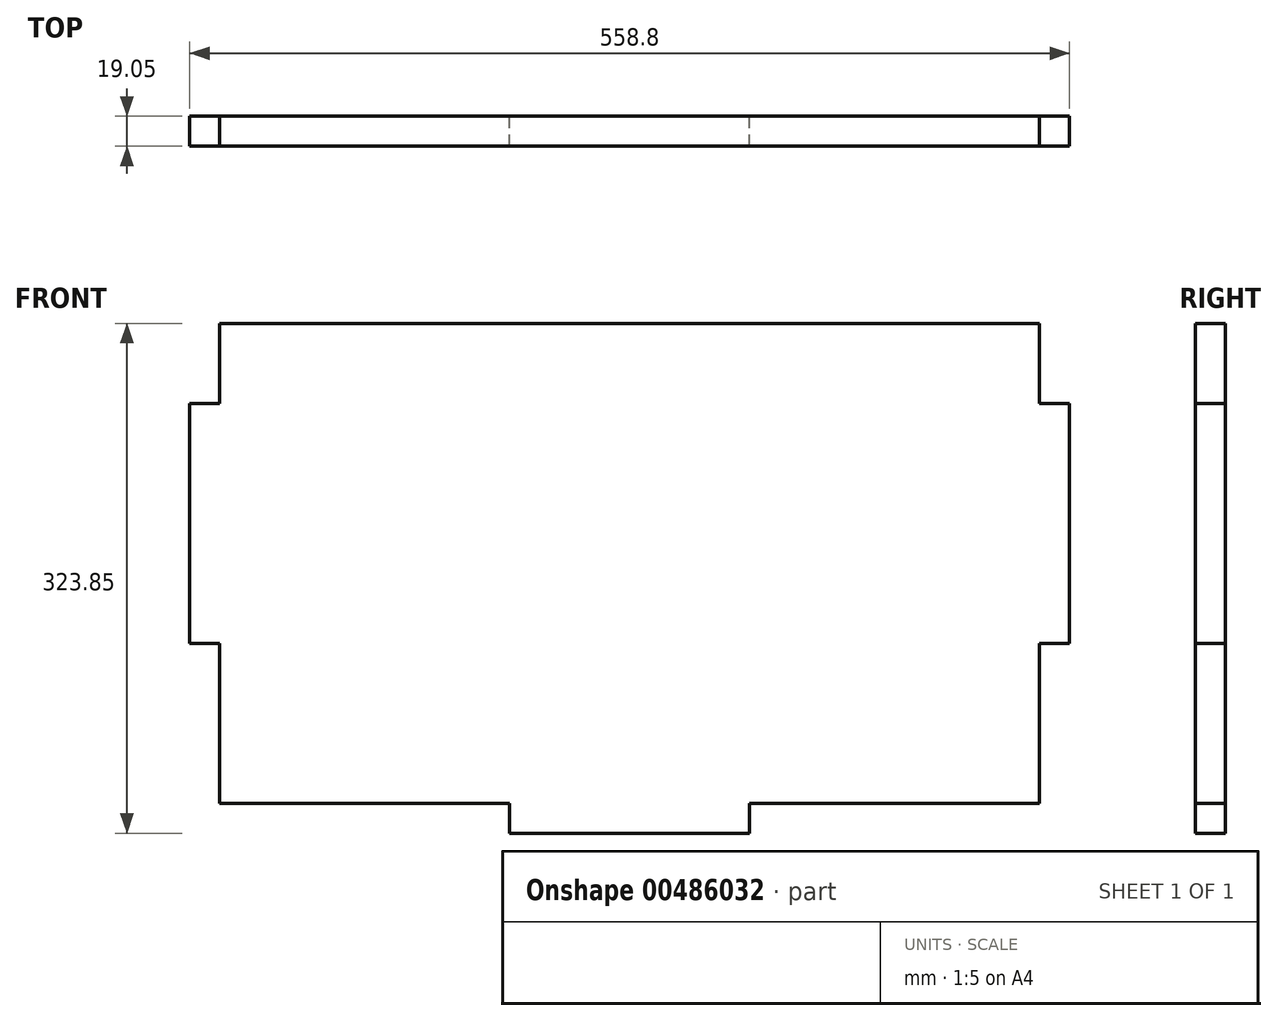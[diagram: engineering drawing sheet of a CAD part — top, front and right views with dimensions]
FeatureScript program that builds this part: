
annotation { "Feature Type Name" : "Feature", "Feature Type Description" : "" }
export const myFeature = defineFeature(function(context is Context, id is Id, definition is map)
    precondition{}
    {
        {
            var Q0;
            Q0=qCreatedBy(makeId("Front.planeOp"),FACE);
            var sketch = newSketch(context, id + "F0", { "sketchPlane" : qUnion([Q0])});
            skLineSegment(sketch, "E0.bottom", {"start": v(-204.8, -103.62) * mm, "end": v(-725.5, -103.62) * mm});
            skLineSegment(sketch, "E0.top", {"start": v(-204.8, 201.18) * mm, "end": v(-725.5, 201.18) * mm});
            skLineSegment(sketch, "E0.left", {"start": v(-204.8, -103.62) * mm, "end": v(-204.8, 201.18) * mm});
            skLineSegment(sketch, "E0.right", {"start": v(-725.5, -103.62) * mm, "end": v(-725.5, 201.18) * mm});
            skLineSegment(sketch, "E1.bottom", {"start": v(-725.5, 150.38) * mm, "end": v(-744.55, 150.38) * mm});
            skLineSegment(sketch, "E1.top", {"start": v(-725.5, -2.02) * mm, "end": v(-744.55, -2.02) * mm});
            skLineSegment(sketch, "E1.left", {"start": v(-725.5, 150.38) * mm, "end": v(-725.5, -2.02) * mm});
            skLineSegment(sketch, "E1.right", {"start": v(-744.55, 150.38) * mm, "end": v(-744.55, -2.02) * mm});
            skLineSegment(sketch, "E2.bottom", {"start": v(-204.8, 150.38) * mm, "end": v(-185.75, 150.38) * mm});
            skLineSegment(sketch, "E2.top", {"start": v(-204.8, -2.02) * mm, "end": v(-185.75, -2.02) * mm});
            skLineSegment(sketch, "E2.left", {"start": v(-204.8, 150.38) * mm, "end": v(-204.8, -2.02) * mm});
            skLineSegment(sketch, "E2.right", {"start": v(-185.75, 150.38) * mm, "end": v(-185.75, -2.02) * mm});
            skLineSegment(sketch, "E3", {"start": v(-204.8, -2.02) * mm, "end": v(-204.8, -103.62) * mm});
            skLineSegment(sketch, "E4", {"start": v(-725.5, -2.02) * mm, "end": v(-725.5, -103.62) * mm});
            skPoint(sketch, "E5.middle", {"position": v(-465.15, -103.62) * mm});
            skLineSegment(sketch, "E6", {"start": v(-725.5, -103.62) * mm, "end": v(-541.35, -103.62) * mm});
            skLineSegment(sketch, "E7", {"start": v(-204.8, -103.62) * mm, "end": v(-388.95, -103.62) * mm});
            skLineSegment(sketch, "E8", {"start": v(-541.35, -103.62) * mm, "end": v(-541.35, -122.67) * mm});
            skLineSegment(sketch, "E9", {"start": v(-541.35, -122.67) * mm, "end": v(-388.95, -122.67) * mm});
            skLineSegment(sketch, "E10", {"start": v(-388.95, -122.67) * mm, "end": v(-388.95, -103.62) * mm});
            skSolve(sketch);
        }
        {
            var Q0;
            {var subQ3=sQuery(id+"F0.wireOp",EDGE,"E0.bottom");Q0=makeQuery(id+"F0.imprint","IMPRINT",FACE,{"disambiguationData":[TD([[makeQuery(id+"F0.imprint","IMPRINT",EDGE,{"derivedFrom":subQ3}),-1.0]])]});}
            var Q1;
            Q1=makeQuery(id+"F0.imprint","IMPRINT",FACE,{"disambiguationData":[TD([[makeQuery(id+"F0.imprint","IMPRINT",EDGE,{"derivedFrom":sQuery(id+"F0.wireOp",EDGE,"E1.bottom")}),1.0]])]});
            var Q2;
            Q2=makeQuery(id+"F0.imprint","IMPRINT",FACE,{"disambiguationData":[TD([[makeQuery(id+"F0.imprint","IMPRINT",EDGE,{"derivedFrom":sQuery(id+"F0.wireOp",EDGE,"E2.bottom")}),-1.0]])]});
            var Q3;
            Q3=makeQuery(id+"F0.imprint","IMPRINT",FACE,{"disambiguationData":[TD([[makeQuery(id+"F0.imprint","IMPRINT",EDGE,{"derivedFrom":sQuery(id+"F0.wireOp",EDGE,"E5.bottom")}),-1.0]])]});
            var Q4;
            Q4=makeQuery(id+"F0.imprint","IMPRINT",FACE,{"disambiguationData":[TD([[makeQuery(id+"F0.imprint","IMPRINT",EDGE,{"derivedFrom":sQuery(id+"F0.wireOp",EDGE,"E0.bottom")}),1.0]])]});
            extrude(context, id + "F1", {"entities" : qUnion([Q0, Q1, Q2, Q3, Q4]), "depth" : 19.05 * mm, "offsetDistance" : 25.4 * mm});
        }
    });
